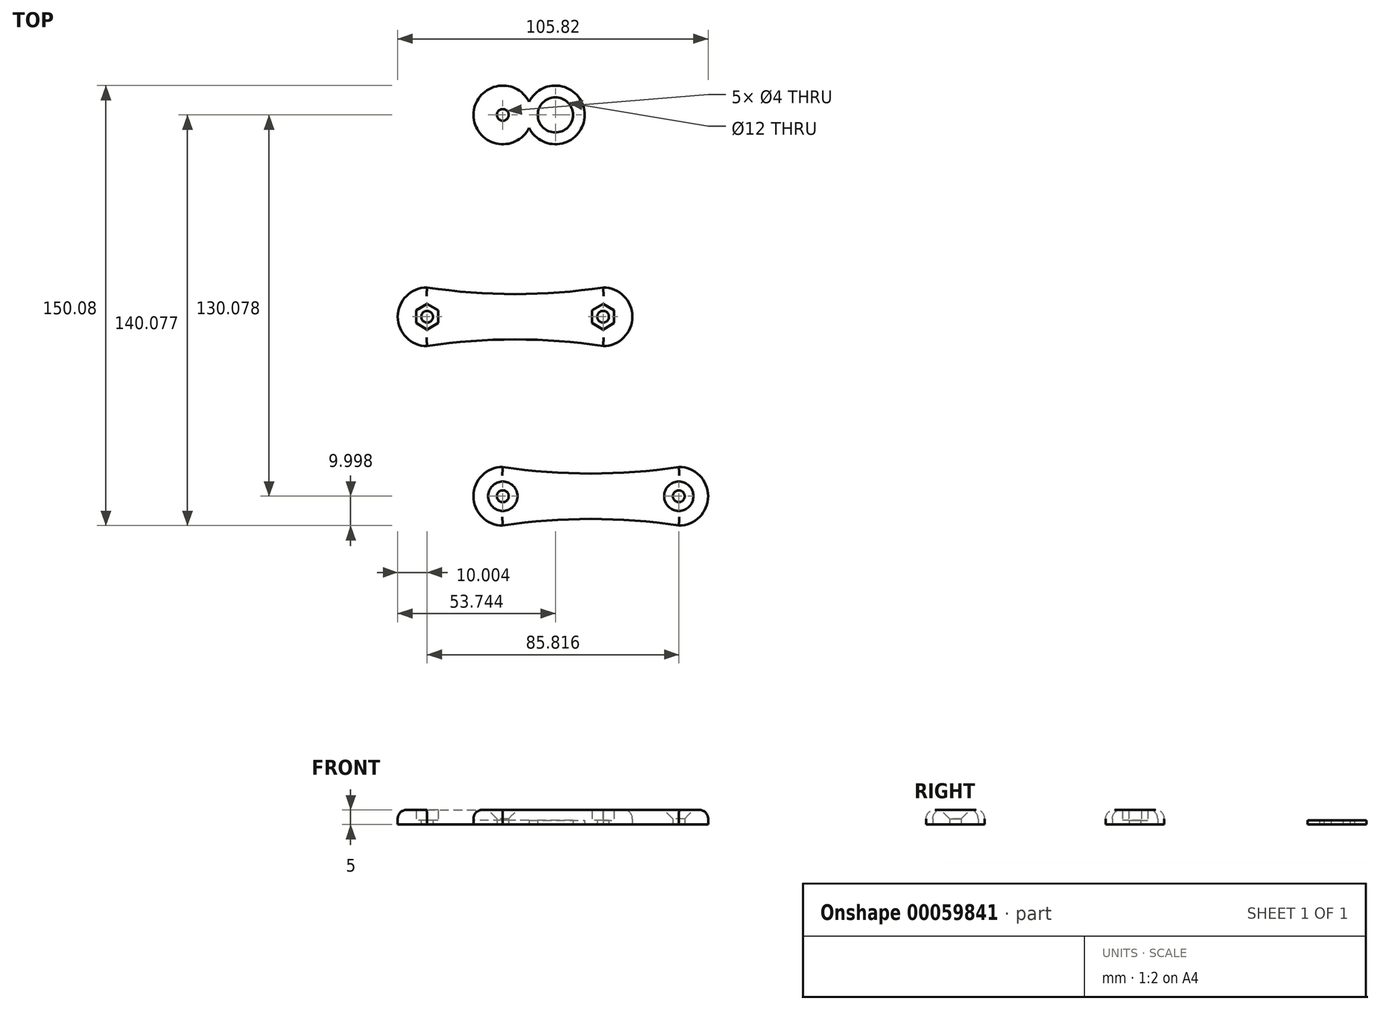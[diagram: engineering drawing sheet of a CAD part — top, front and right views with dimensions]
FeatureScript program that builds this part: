
annotation { "Feature Type Name" : "Feature", "Feature Type Description" : "" }
export const myFeature = defineFeature(function(context is Context, id is Id, definition is map)
    precondition{}
    {
        {
            var Q0;
            Q0=qCreatedBy(makeId("Top.planeOp"),FACE);
            var sketch = newSketch(context, id + "F3", { "sketchPlane" : qUnion([Q0])});
            skLineSegment(sketch, "E0", {"start": v(0, -18.63) * mm, "end": v(60, -18.63) * mm, "construction": true});
            skCircle(sketch, "E1", {"center": v(0, -18.63) * mm, "radius": 2 * mm});
            skCircle(sketch, "E2", {"center": v(60, -18.63) * mm, "radius": 2 * mm});
            skArc(sketch, "E3", {"start": v(0, -8.63) * mm, "mid": v(-10, -18.63) * mm, "end": v(0, -28.63) * mm});
            skArc(sketch, "E4", {"start": v(60, -28.63) * mm, "mid": v(70, -18.63) * mm, "end": v(60, -8.63) * mm});
            skArc(sketch, "E5", {"start": v(0, -8.63) * mm, "mid": v(30, -10.9) * mm, "end": v(60, -8.63) * mm});
            skArc(sketch, "E6.MirrorCS", {"start": v(0, -28.63) * mm, "mid": v(30, -26.37) * mm, "end": v(60, -28.63) * mm});
            skLineSegment(sketch, "E7", {"start": v(-25.82, 42.6) * mm, "end": v(34.18, 42.6) * mm, "construction": true});
            skCircle(sketch, "E8", {"center": v(-25.82, 42.6) * mm, "radius": 2 * mm});
            skCircle(sketch, "E9", {"center": v(34.18, 42.6) * mm, "radius": 2 * mm});
            skArc(sketch, "E10", {"start": v(-25.82, 52.6) * mm, "mid": v(-35.82, 42.6) * mm, "end": v(-25.82, 32.6) * mm});
            skArc(sketch, "E11", {"start": v(34.18, 32.6) * mm, "mid": v(44.18, 42.6) * mm, "end": v(34.18, 52.6) * mm});
            skArc(sketch, "E12", {"start": v(-25.82, 52.6) * mm, "mid": v(4.18, 50.33) * mm, "end": v(34.18, 52.6) * mm});
            skArc(sketch, "E13.MirrorCS", {"start": v(-25.82, 32.6) * mm, "mid": v(4.18, 34.85) * mm, "end": v(34.18, 32.6) * mm});
            skCircle(sketch, "E14.cCircle", {"center": v(-25.82, 42.6) * mm, "radius": 3.75 * mm, "construction": true});
            skLineSegment(sketch, "E14.0", {"start": v(-22.07, 40.43) * mm, "end": v(-25.82, 38.26) * mm});
            skLineSegment(sketch, "E14.1", {"start": v(-25.82, 38.26) * mm, "end": v(-29.57, 40.43) * mm});
            skLineSegment(sketch, "E14.2", {"start": v(-29.57, 40.43) * mm, "end": v(-29.57, 44.76) * mm});
            skLineSegment(sketch, "E14.3", {"start": v(-29.57, 44.76) * mm, "end": v(-25.82, 46.92) * mm});
            skLineSegment(sketch, "E14.4", {"start": v(-25.82, 46.92) * mm, "end": v(-22.07, 44.76) * mm});
            skLineSegment(sketch, "E14.5", {"start": v(-22.07, 44.76) * mm, "end": v(-22.07, 40.43) * mm});
            skPoint(sketch, "E14.0.midPoint", {"position": v(-23.94, 39.34) * mm});
            skCircle(sketch, "E15.cCircle", {"center": v(34.18, 42.6) * mm, "radius": 3.75 * mm, "construction": true});
            skLineSegment(sketch, "E15.0", {"start": v(37.93, 44.76) * mm, "end": v(37.93, 40.43) * mm});
            skLineSegment(sketch, "E15.1", {"start": v(37.93, 40.43) * mm, "end": v(34.18, 38.26) * mm});
            skLineSegment(sketch, "E15.2", {"start": v(34.18, 38.26) * mm, "end": v(30.43, 40.43) * mm});
            skLineSegment(sketch, "E15.3", {"start": v(30.43, 40.43) * mm, "end": v(30.43, 44.76) * mm});
            skLineSegment(sketch, "E15.4", {"start": v(30.43, 44.76) * mm, "end": v(34.18, 46.92) * mm});
            skLineSegment(sketch, "E15.5", {"start": v(34.18, 46.92) * mm, "end": v(37.93, 44.76) * mm});
            skPoint(sketch, "E15.0.midPoint", {"position": v(37.93, 42.6) * mm});
            skArc(sketch, "E16", {"start": v(8.96, 115.88) * mm, "mid": v(-10, 111.45) * mm, "end": v(8.96, 107) * mm});
            skArc(sketch, "E17", {"start": v(8.96, 107) * mm, "mid": v(27.92, 111.45) * mm, "end": v(8.96, 115.88) * mm});
            skCircle(sketch, "E18", {"center": v(0, 111.45) * mm, "radius": 2 * mm});
            skCircle(sketch, "E19", {"center": v(17.92, 111.45) * mm, "radius": 6 * mm});
            skPoint(sketch, "E20", {"position": v(17.92, 117.45) * mm});
            skPoint(sketch, "E21", {"position": v(17.92, 121.45) * mm});
            skSolve(sketch);
        }
        {
            var Q0;
            Q0=makeQuery(id+"F3.imprint","IMPRINT",FACE,{"disambiguationData":[TD([[makeQuery(id+"F3.imprint","IMPRINT",EDGE,{"derivedFrom":sQuery(id+"F3.wireOp",EDGE,"E1")}),-1.0]])]});
            var Q1;
            Q1=makeQuery(id+"F3.imprint","IMPRINT",FACE,{"disambiguationData":[TD([[makeQuery(id+"F3.imprint","IMPRINT",EDGE,{"derivedFrom":sQuery(id+"F3.wireOp",EDGE,"E10")}),1.0]])]});
            extrude(context, id + "F0", {"entities" : qUnion([Q0, Q1]), "depth" : 5 * mm});
        }
        {
            var Q0;
            Q0=makeQuery(id+"F0.opExtrude","CAP_EDGE",EDGE,{"disambiguationData":[OSD([sQuery(id+"F3.wireOp",EDGE,"E13.MirrorCS")])],"isStart":false});
            var Q1;
            Q1=makeQuery(id+"F0.opExtrude","CAP_EDGE",EDGE,{"disambiguationData":[OSD([sQuery(id+"F3.wireOp",EDGE,"E11")])],"isStart":false});
            var Q2;
            Q2=makeQuery(id+"F0.opExtrude","CAP_EDGE",EDGE,{"disambiguationData":[OSD([sQuery(id+"F3.wireOp",EDGE,"E12")])],"isStart":false});
            var Q3;
            Q3=makeQuery(id+"F0.opExtrude","CAP_EDGE",EDGE,{"disambiguationData":[OSD([sQuery(id+"F3.wireOp",EDGE,"E5")])],"isStart":false});
            var Q4;
            Q4=makeQuery(id+"F0.opExtrude","CAP_EDGE",EDGE,{"disambiguationData":[OSD([sQuery(id+"F3.wireOp",EDGE,"E3")])],"isStart":false});
            var Q5;
            Q5=makeQuery(id+"F0.opExtrude","CAP_EDGE",EDGE,{"disambiguationData":[OSD([sQuery(id+"F3.wireOp",EDGE,"E6.MirrorCS")])],"isStart":false});
            var Q6;
            Q6=makeQuery(id+"F0.opExtrude","CAP_EDGE",EDGE,{"disambiguationData":[OSD([sQuery(id+"F3.wireOp",EDGE,"E4")])],"isStart":false});
            var Q7;
            Q7=makeQuery(id+"F0.opExtrude","CAP_EDGE",EDGE,{"disambiguationData":[OSD([sQuery(id+"F3.wireOp",EDGE,"E10")])],"isStart":false});
            fillet(context, id + "F4", {"entities" : qUnion([Q0, Q1, Q2, Q3, Q4, Q5, Q6, Q7]), "radius" : 3 * mm, "tangentPropagation" : true, "allowEdgeOverflow" : false});
        }
        {
            var Q0;
            Q0=makeQuery(id+"F0.opExtrude","CAP_EDGE",EDGE,{"disambiguationData":[OSD([sQuery(id+"F3.wireOp",EDGE,"E2")])],"isStart":false});
            var Q1;
            Q1=makeQuery(id+"F0.opExtrude","CAP_EDGE",EDGE,{"disambiguationData":[OSD([sQuery(id+"F3.wireOp",EDGE,"E1")])],"isStart":false});
            chamfer(context, id + "F1", {"entities" : qUnion([Q0, Q1]), "width" : 3 * mm, "tangentPropagation" : true});
        }
        {
            var Q0;
            Q0=makeQuery(id+"F3.imprint","IMPRINT",FACE,{"disambiguationData":[TD([[makeQuery(id+"F3.imprint","IMPRINT",EDGE,{"derivedFrom":sQuery(id+"F3.wireOp",EDGE,"E9")}),-1.0]])]});
            var Q1;
            Q1=makeQuery(id+"F3.imprint","IMPRINT",FACE,{"disambiguationData":[TD([[makeQuery(id+"F3.imprint","IMPRINT",EDGE,{"derivedFrom":sQuery(id+"F3.wireOp",EDGE,"E8")}),-1.0]])]});
            var Q2;
            Q2=makeQuery(id+"F3.imprint","IMPRINT",FACE,{"disambiguationData":[TD([[makeQuery(id+"F3.imprint","IMPRINT",EDGE,{"derivedFrom":sQuery(id+"F3.wireOp",EDGE,"E16")}),1.0]])]});
            extrude(context, id + "F2", {"entities" : qUnion([Q0, Q1, Q2]), "operationType" : NewBodyOperationType.ADD, "depth" : 1.5 * mm});
        }
    });
